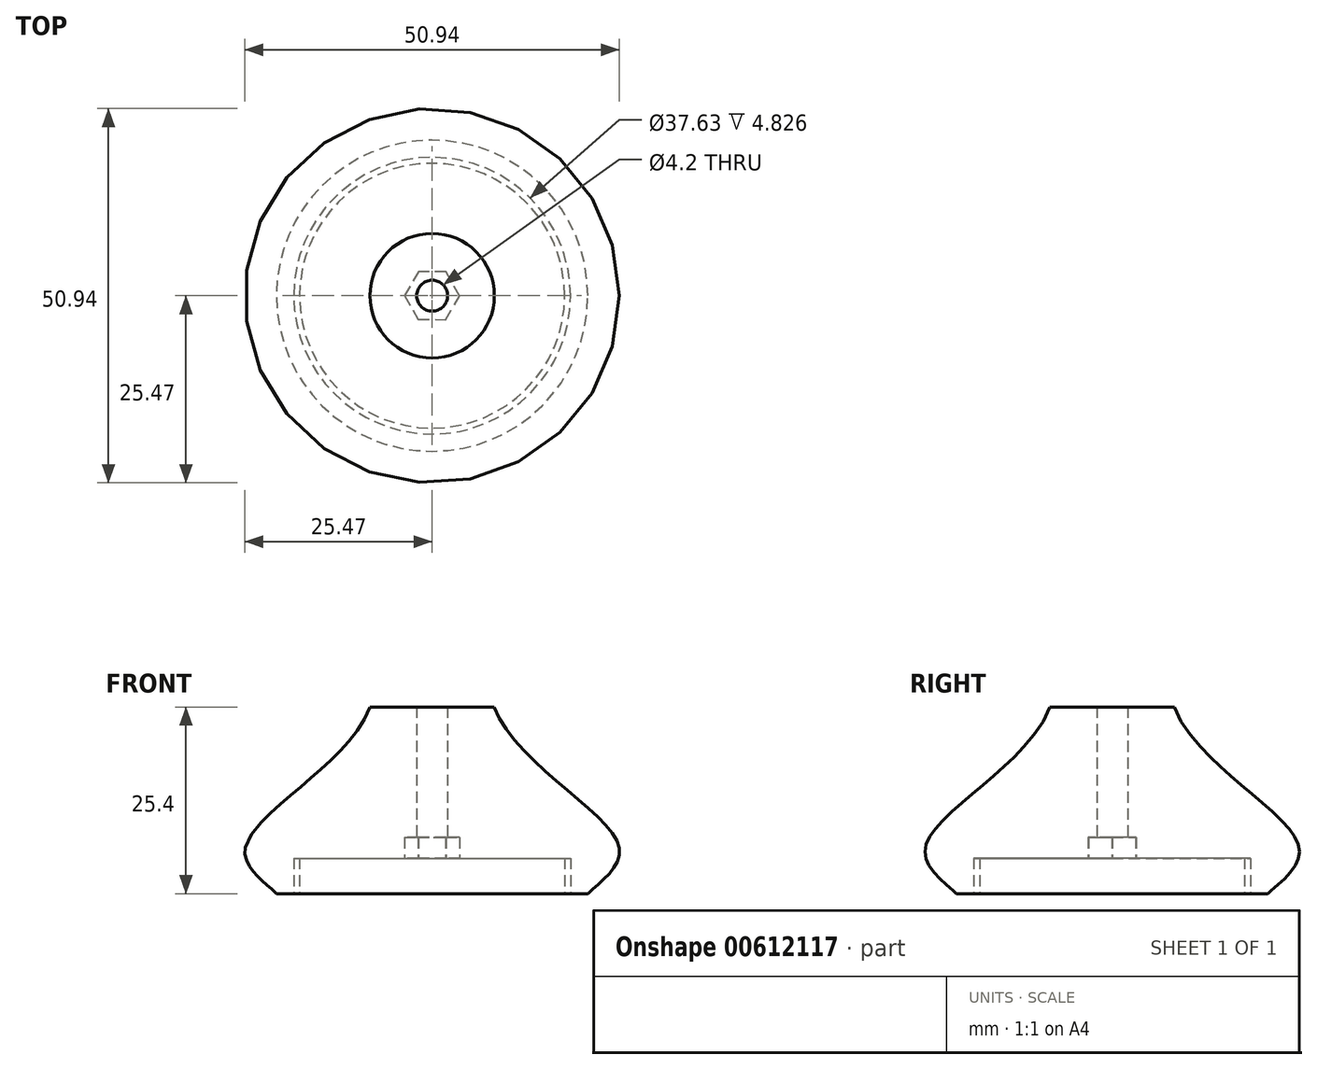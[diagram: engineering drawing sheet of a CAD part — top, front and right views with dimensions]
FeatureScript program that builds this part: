
annotation { "Feature Type Name" : "Feature", "Feature Type Description" : "" }
export const myFeature = defineFeature(function(context is Context, id is Id, definition is map)
    precondition{}
    {
        {
            var Q0;
            Q0=qCreatedBy(makeId("Front.planeOp"),FACE);
            var sketch = newSketch(context, id + "F0", { "sketchPlane" : qUnion([Q0])});
            skLineSegment(sketch, "E0", {"start": v(0, 0) * mm, "end": v(21.17, 0) * mm});
            skFitSpline(sketch, "E1", {"points": [v(21.17, 0) * mm, v(25.4, 6.35) * mm, v(8.47, 25.4) * mm], "startDerivative": vector(14.44, 13.72) * mm, "endDerivative": vector(-12.38, 35.41) * mm});
            skLineSegment(sketch, "E2", {"start": v(8.47, 25.4) * mm, "end": v(0, 25.4) * mm});
            skLineSegment(sketch, "E3", {"start": v(0, 25.4) * mm, "end": v(0, 0) * mm});
            skSolve(sketch);
        }
        {
            var Q0;
            Q0 = qSketchRegion(id + "F0", true);
            var Q1;
            Q1=sQuery(id+"F0.wireOp",EDGE,"E3");
            revolve(context, id + "F1", {"entities" : qUnion([Q0]), "axis" : qUnion([Q1]), "revolveType" : RevolveType.FULL});
        }
        {
            var Q0;
            Q0=makeQuery(id+"F1.opRevolve","SWEPT_FACE",FACE,{"disambiguationData":[OSD([sQuery(id+"F0.wireOp",EDGE,"E0")])]});
            var sketch = newSketch(context, id + "F2", { "sketchPlane" : qUnion([Q0])});
            skCircle(sketch, "E4.0", {"center": v(0, 0) * mm, "radius": 18.82 * mm});
            skSolve(sketch);
        }
        {
            var Q0;
            Q0 = qSketchRegion(id + "F2", true);
            extrude(context, id + "F3", {"entities" : qUnion([Q0]), "operationType" : NewBodyOperationType.REMOVE, "oppositeDirection" : true, "depth" : 4.83 * mm, "offsetDistance" : 25.4 * mm});
        }
        {
            var Q0;
            Q0=makeQuery(id+"F2.imprint","IMPRINT",FACE,{"disambiguationData":[TD([[makeQuery(id+"F2.imprint","IMPRINT",EDGE,{"derivedFrom":sQuery(id+"F2.wireOp",EDGE,"E4.0")}),-1.0]])]});
            var sketch = newSketch(context, id + "F4", { "sketchPlane" : qUnion([Q0])});
            skCircle(sketch, "E5.cCircle", {"center": v(0, 0) * mm, "radius": 3.75 * mm, "construction": true});
            skLineSegment(sketch, "E5.0", {"start": v(1.85, 3.26) * mm, "end": v(3.75, 0.02) * mm});
            skLineSegment(sketch, "E5.1", {"start": v(3.75, 0.02) * mm, "end": v(1.9, -3.23) * mm});
            skLineSegment(sketch, "E5.2", {"start": v(1.9, -3.23) * mm, "end": v(-1.85, -3.26) * mm});
            skLineSegment(sketch, "E5.3", {"start": v(-1.85, -3.26) * mm, "end": v(-3.75, -0.02) * mm});
            skLineSegment(sketch, "E5.4", {"start": v(-3.75, -0.02) * mm, "end": v(-1.9, 3.23) * mm});
            skLineSegment(sketch, "E5.5", {"start": v(-1.9, 3.23) * mm, "end": v(1.85, 3.26) * mm});
            skSolve(sketch);
        }
        {
            var Q0;
            Q0 = qSketchRegion(id + "F4", true);
            extrude(context, id + "F5", {"entities" : qUnion([Q0]), "operationType" : NewBodyOperationType.REMOVE, "oppositeDirection" : true, "depth" : 7.65 * mm, "offsetDistance" : 25.4 * mm});
        }
        {
            var Q0;
            Q0=makeQuery(id+"F5.boolean.opBoolean","COPY",FACE,{"derivedFrom":makeQuery(id+"F5.opExtrude","CAP_FACE",FACE,{"disambiguationData":[OSD([sQuery(id+"F4.wireOp",EDGE,"E5.0"),sQuery(id+"F4.wireOp",EDGE,"E5.1"),sQuery(id+"F4.wireOp",EDGE,"E5.2"),sQuery(id+"F4.wireOp",EDGE,"E5.3"),sQuery(id+"F4.wireOp",EDGE,"E5.4"),sQuery(id+"F4.wireOp",EDGE,"E5.5")])],"isStart":false})});
            var sketch = newSketch(context, id + "F6", { "sketchPlane" : qUnion([Q0])});
            skCircle(sketch, "E6", {"center": v(0, 0) * mm, "radius": 2.1 * mm});
            skSolve(sketch);
        }
        {
            var Q0;
            Q0=makeQuery(id+"F6.imprint","IMPRINT",FACE,{"disambiguationData":[TD([[makeQuery(id+"F6.imprint","IMPRINT",EDGE,{"derivedFrom":sQuery(id+"F6.wireOp",EDGE,"E6")}),1.0]])]});
            extrude(context, id + "F7", {"entities" : qUnion([Q0]), "operationType" : NewBodyOperationType.REMOVE, "endBound" : BoundingType.THROUGH_ALL, "oppositeDirection" : true, "depth" : 25.4 * mm, "offsetDistance" : 25.4 * mm});
        }
        {
            var Q0;
            Q0=makeQuery(id+"F1.opRevolve","SWEPT_FACE",FACE,{"disambiguationData":[OSD([sQuery(id+"F0.wireOp",EDGE,"E0")])]});
            var sketch = newSketch(context, id + "F8", { "sketchPlane" : qUnion([Q0])});
            skCircle(sketch, "E7.0", {"center": v(0, 0) * mm, "radius": 18.82 * mm});
            skCircle(sketch, "E8.0", {"center": v(0, 0) * mm, "radius": 18.02 * mm});
            skSolve(sketch);
        }
        {
            var Q0;
            Q0=makeQuery(id+"F8.imprint","IMPRINT",FACE,{"disambiguationData":[TD([[makeQuery(id+"F8.imprint","IMPRINT",EDGE,{"derivedFrom":sQuery(id+"F8.wireOp",EDGE,"E8.0")}),1.0]])]});
            var Q1;
            Q1=makeQuery(id+"F3.boolean.opBoolean","COPY",FACE,{"derivedFrom":makeQuery(id+"F3.opExtrude","CAP_FACE",FACE,{"disambiguationData":[OSD([sQuery(id+"F2.wireOp",EDGE,"E4.0")])],"isStart":false})});
            extrude(context, id + "F9", {"entities" : qUnion([Q0]), "endBound" : BoundingType.UP_TO_SURFACE, "oppositeDirection" : true, "depth" : 25.4 * mm, "endBoundEntityFace" : qUnion([Q1]), "offsetDistance" : 25.4 * mm});
        }
    });
